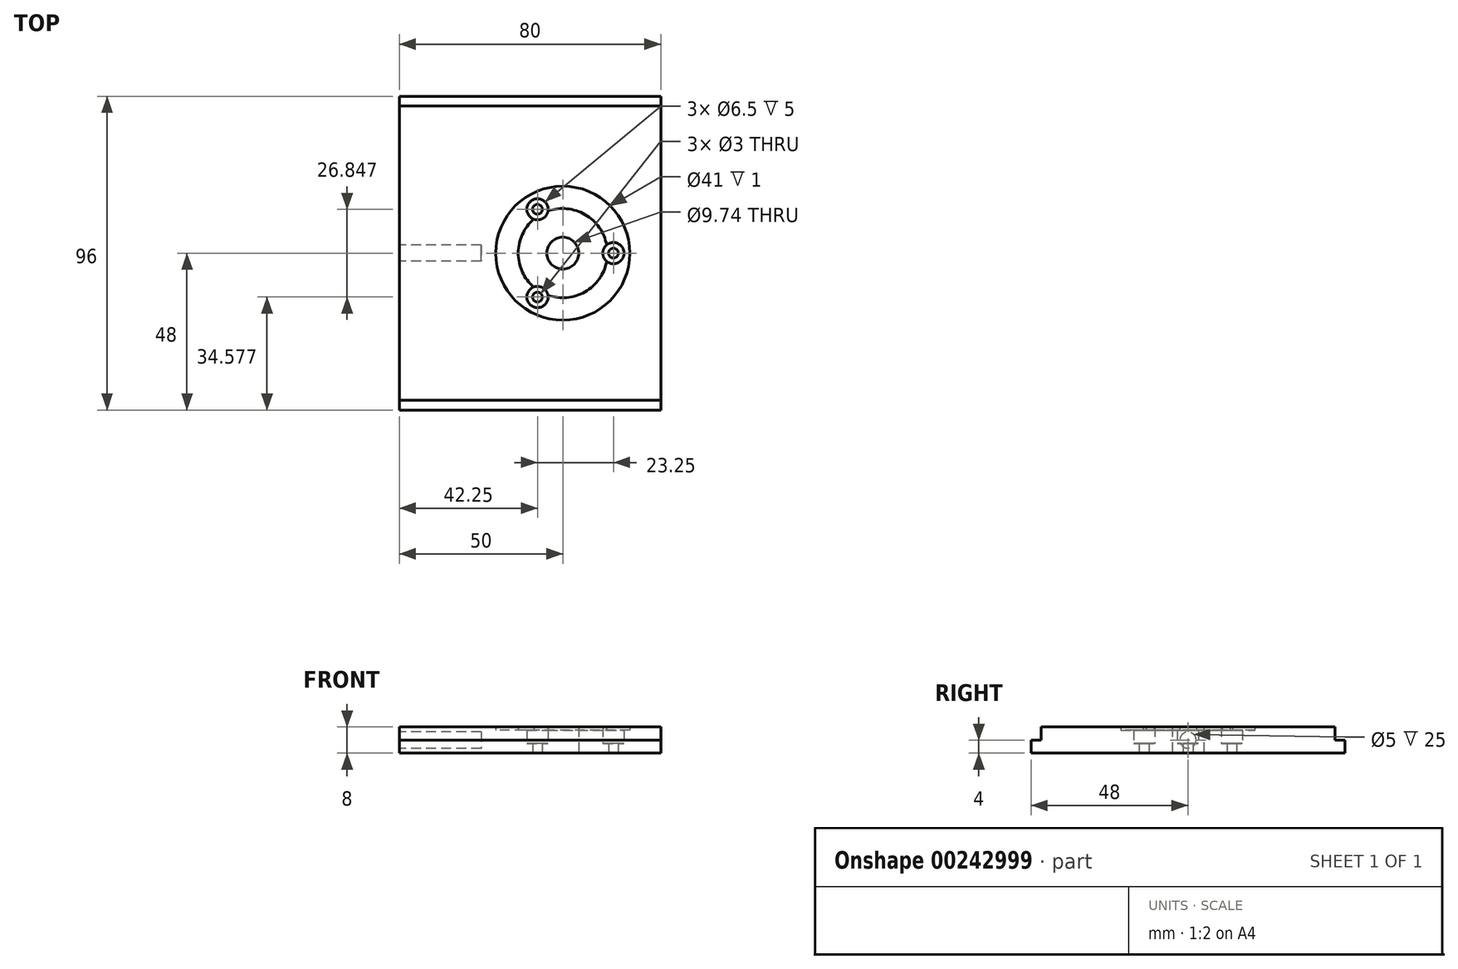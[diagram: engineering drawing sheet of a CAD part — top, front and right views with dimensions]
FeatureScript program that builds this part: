
annotation { "Feature Type Name" : "Feature", "Feature Type Description" : "" }
export const myFeature = defineFeature(function(context is Context, id is Id, definition is map)
    precondition{}
    {
        {
            var Q0;
            Q0=qCreatedBy(makeId("Top.planeOp"),FACE);
            var sketch = newSketch(context, id + "F0", { "sketchPlane" : qUnion([Q0])});
            skLineSegment(sketch, "E0.bottom", {"start": v(-50, 48) * mm, "end": v(30, 48) * mm});
            skLineSegment(sketch, "E0.top", {"start": v(-50, -48) * mm, "end": v(30, -48) * mm});
            skLineSegment(sketch, "E0.left", {"start": v(-50, 48) * mm, "end": v(-50, -48) * mm});
            skLineSegment(sketch, "E0.right", {"start": v(30, 48) * mm, "end": v(30, -48) * mm});
            skPoint(sketch, "E1", {"position": v(-50, 0) * mm});
            skCircle(sketch, "E2", {"center": v(0, 0) * mm, "radius": 4.87 * mm});
            skCircle(sketch, "E3", {"center": v(0, 0) * mm, "radius": 15.5 * mm, "construction": true});
            skCircle(sketch, "E4", {"center": v(15.5, 0) * mm, "radius": 1.5 * mm});
            skCircle(sketch, "E5", {"center": v(-7.75, 13.42) * mm, "radius": 1.5 * mm});
            skCircle(sketch, "E6", {"center": v(-7.75, -13.42) * mm, "radius": 1.5 * mm});
            skLineSegment(sketch, "E7", {"start": v(0, 0) * mm, "end": v(-7.75, -13.42) * mm, "construction": true});
            skLineSegment(sketch, "E8", {"start": v(0, 0) * mm, "end": v(-7.75, 13.42) * mm, "construction": true});
            skCircle(sketch, "E9", {"center": v(0, 0) * mm, "radius": 20.5 * mm});
            skCircle(sketch, "E10", {"center": v(0, 0) * mm, "radius": 13.65 * mm});
            skCircle(sketch, "E11", {"center": v(-7.75, 13.42) * mm, "radius": 3.25 * mm});
            skCircle(sketch, "E12", {"center": v(15.5, 0) * mm, "radius": 3.25 * mm});
            skCircle(sketch, "E13", {"center": v(-7.75, -13.42) * mm, "radius": 3.25 * mm});
            skSolve(sketch);
        }
        {
            var Q0;
            Q0 = qSketchRegion(id + "F0", true);
            var Q1;
            Q1=makeQuery(id+"F0.imprint","IMPRINT",FACE,{"disambiguationData":[TD([[makeQuery(id+"F0.imprint","IMPRINT",EDGE,{"derivedFrom":sQuery(id+"F0.wireOp",EDGE,"E2")}),-1.0]])]});
            extrude(context, id + "F1", {"entities" : qUnion([Q0, Q1]), "depth" : 8 * mm});
        }
        {
            var Q0;
            Q0=makeQuery(id+"F0.imprint","IMPRINT",FACE,{"disambiguationData":[TD([[makeQuery(id+"F0.imprint","IMPRINT",EDGE,{"derivedFrom":sQuery(id+"F0.wireOp",EDGE,"E9")}),1.0]])]});
            extrude(context, id + "F2", {"entities" : qUnion([Q0]), "operationType" : NewBodyOperationType.ADD, "depth" : 7 * mm});
        }
        {
            var Q0;
            Q0=makeQuery(id+"F0.imprint","IMPRINT",FACE,{"disambiguationData":[TD([[makeQuery(id+"F0.imprint","IMPRINT",EDGE,{"derivedFrom":sQuery(id+"F0.wireOp",EDGE,"E6")}),-1.0]])]});
            var Q1;
            {var subQ0=sQuery(id+"F0.wireOp",EDGE,"E13");var subQ1=sQuery(id+"F0.wireOp",EDGE,"E10");var subQ2=makeQuery(id+"F0.imprint","INTERSECT",VERTEX,{"disambiguationData":[OD(0.0)],"derivedFrom":[subQ1,subQ0]});Q1=makeQuery(id+"F0.imprint","IMPRINT",FACE,{"disambiguationData":[TD([[makeQuery(id+"F0.imprint","IMPRINT",EDGE,{"disambiguationData":[TD([[subQ2,-1.0]])],"derivedFrom":subQ1}),1.0]])]});}
            var Q2;
            Q2=makeQuery(id+"F0.imprint","IMPRINT",FACE,{"disambiguationData":[TD([[makeQuery(id+"F0.imprint","IMPRINT",EDGE,{"derivedFrom":sQuery(id+"F0.wireOp",EDGE,"E4")}),-1.0]])]});
            var Q3;
            {var subQ0=sQuery(id+"F0.wireOp",EDGE,"E12");var subQ1=sQuery(id+"F0.wireOp",EDGE,"E10");var subQ2=makeQuery(id+"F0.imprint","INTERSECT",VERTEX,{"disambiguationData":[OD(0.0)],"derivedFrom":[subQ1,subQ0]});Q3=makeQuery(id+"F0.imprint","IMPRINT",FACE,{"disambiguationData":[TD([[makeQuery(id+"F0.imprint","IMPRINT",EDGE,{"disambiguationData":[TD([[subQ2,1.0]])],"derivedFrom":subQ1}),1.0]])]});}
            var Q4;
            Q4=makeQuery(id+"F0.imprint","IMPRINT",FACE,{"disambiguationData":[TD([[makeQuery(id+"F0.imprint","IMPRINT",EDGE,{"derivedFrom":sQuery(id+"F0.wireOp",EDGE,"E5")}),-1.0]])]});
            var Q5;
            {var subQ0=sQuery(id+"F0.wireOp",EDGE,"E11");var subQ1=sQuery(id+"F0.wireOp",EDGE,"E10");var subQ2=makeQuery(id+"F0.imprint","INTERSECT",VERTEX,{"disambiguationData":[OD(0.0)],"derivedFrom":[subQ1,subQ0]});Q5=makeQuery(id+"F0.imprint","IMPRINT",FACE,{"disambiguationData":[TD([[makeQuery(id+"F0.imprint","IMPRINT",EDGE,{"disambiguationData":[TD([[subQ2,-1.0]])],"derivedFrom":subQ1}),1.0]])]});}
            extrude(context, id + "F3", {"entities" : qUnion([Q0, Q1, Q2, Q3, Q4, Q5]), "operationType" : NewBodyOperationType.ADD, "depth" : 3 * mm});
        }
        {
            var Q0;
            Q0=makeQuery(id+"F1.opExtrude","SWEPT_FACE",FACE,{"disambiguationData":[OSD([sQuery(id+"F0.wireOp",EDGE,"E0.left")])]});
            var sketch = newSketch(context, id + "F4", { "sketchPlane" : qUnion([Q0])});
            skCircle(sketch, "E14", {"center": v(0, 4) * mm, "radius": 2.5 * mm});
            skSolve(sketch);
        }
        {
            var Q0;
            Q0=makeQuery(id+"F4.imprint","IMPRINT",FACE,{"disambiguationData":[TD([[makeQuery(id+"F4.imprint","IMPRINT",EDGE,{"derivedFrom":sQuery(id+"F4.wireOp",EDGE,"N62OyYMt-GJVm-ddj2-uf75-h3XFGl5llLdS")}),1.0]])]});
            var Q1;
            Q1=makeQuery(id+"F4.imprint","IMPRINT",FACE,{"disambiguationData":[TD([[makeQuery(id+"F4.imprint","IMPRINT",EDGE,{"derivedFrom":sQuery(id+"F4.wireOp",EDGE,"E14")}),1.0]])]});
            extrude(context, id + "F5", {"entities" : qUnion([Q0, Q1]), "operationType" : NewBodyOperationType.REMOVE, "oppositeDirection" : true, "depth" : 25 * mm});
        }
        {
            var Q0;
            Q0=makeQuery(id+"F1.opExtrude","SWEPT_FACE",FACE,{"disambiguationData":[OSD([sQuery(id+"F0.wireOp",EDGE,"E0.left")])]});
            var sketch = newSketch(context, id + "F6", { "sketchPlane" : qUnion([Q0])});
            skLineSegment(sketch, "E15.bottom", {"start": v(45, 13.65) * mm, "end": v(48, 13.65) * mm});
            skLineSegment(sketch, "E15.top", {"start": v(45, 4) * mm, "end": v(48, 4) * mm});
            skLineSegment(sketch, "E15.left", {"start": v(45, 13.65) * mm, "end": v(45, 4) * mm});
            skLineSegment(sketch, "E15.right", {"start": v(48, 13.65) * mm, "end": v(48, 4) * mm});
            skLineSegment(sketch, "E16.bottom", {"start": v(-48, 4) * mm, "end": v(-45, 4) * mm});
            skLineSegment(sketch, "E16.top", {"start": v(-48, 16.83) * mm, "end": v(-45, 16.83) * mm});
            skLineSegment(sketch, "E16.left", {"start": v(-48, 4) * mm, "end": v(-48, 16.83) * mm});
            skLineSegment(sketch, "E16.right", {"start": v(-45, 4) * mm, "end": v(-45, 16.83) * mm});
            skSolve(sketch);
        }
        {
            var Q0;
            Q0 = qSketchRegion(id + "F6", true);
            extrude(context, id + "F7", {"entities" : qUnion([Q0]), "operationType" : NewBodyOperationType.REMOVE, "oppositeDirection" : true, "depth" : 100 * mm});
        }
    });
